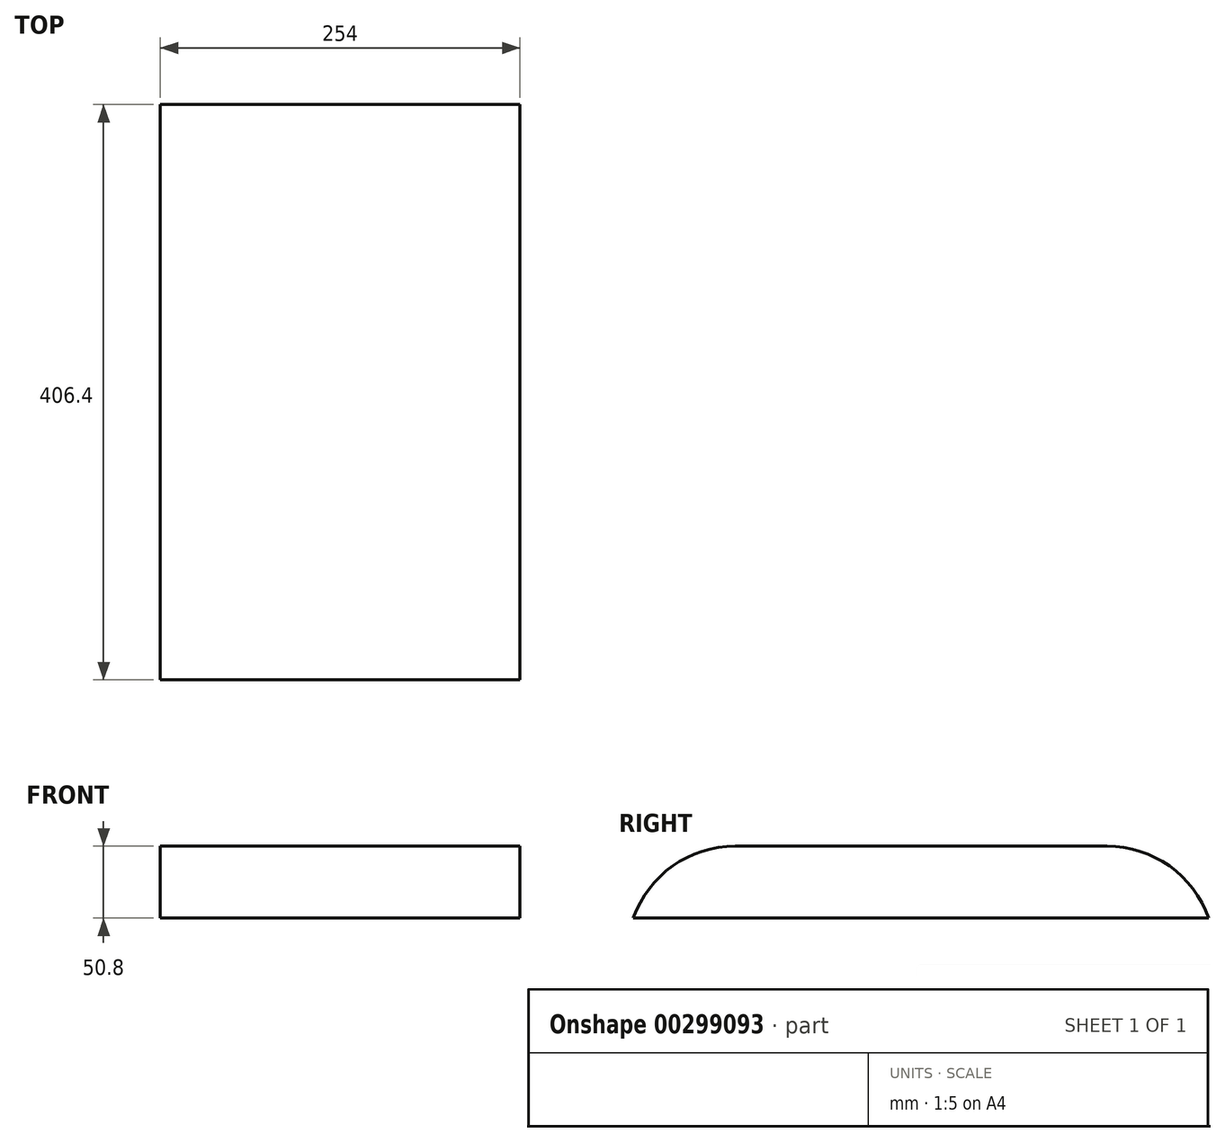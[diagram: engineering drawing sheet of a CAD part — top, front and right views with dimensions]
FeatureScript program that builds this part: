
annotation { "Feature Type Name" : "Feature", "Feature Type Description" : "" }
export const myFeature = defineFeature(function(context is Context, id is Id, definition is map)
    precondition{}
    {
        {
            var Q0;
            Q0=qCreatedBy(makeId("Top.planeOp"),FACE);
            var sketch = newSketch(context, id + "F0", { "sketchPlane" : qUnion([Q0])});
            skLineSegment(sketch, "E0.bottom", {"start": v(-127, 203.2) * mm, "end": v(127, 203.2) * mm});
            skLineSegment(sketch, "E0.top", {"start": v(-127, -203.2) * mm, "end": v(127, -203.2) * mm});
            skLineSegment(sketch, "E0.left", {"start": v(-127, 203.2) * mm, "end": v(-127, -203.2) * mm});
            skLineSegment(sketch, "E0.right", {"start": v(127, 203.2) * mm, "end": v(127, -203.2) * mm});
            skPoint(sketch, "E0.middle", {"position": v(0, 0) * mm});
            skSolve(sketch);
        }
        {
            var Q0;
            Q0 = qSketchRegion(id + "F0", true);
            extrude(context, id + "F1", {"entities" : qUnion([Q0]), "endBound" : BoundingType.SYMMETRIC, "depth" : 50.8 * mm});
        }
        {
            var Q0;
            Q0=makeQuery(id+"F1.opExtrude","CAP_EDGE",EDGE,{"disambiguationData":[OSD([sQuery(id+"F0.wireOp",EDGE,"E0.bottom")])],"isStart":false});
            var Q1;
            Q1=makeQuery(id+"F1.opExtrude","CAP_EDGE",EDGE,{"disambiguationData":[OSD([sQuery(id+"F0.wireOp",EDGE,"E0.top")])],"isStart":false});
            fillet(context, id + "F2", {"entities" : qUnion([Q0, Q1]), "radius" : 76.2 * mm, "tangentPropagation" : true, "allowEdgeOverflow" : false});
        }
    });
